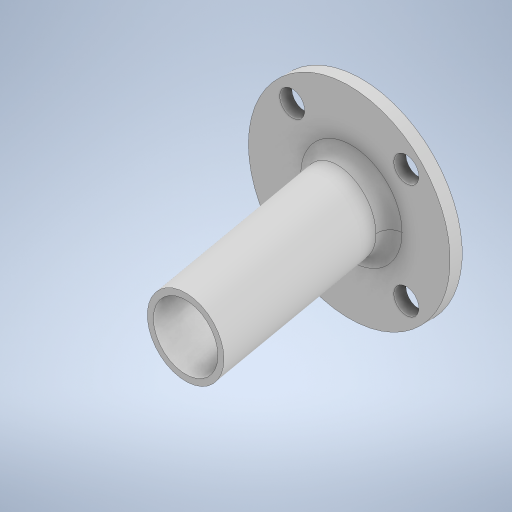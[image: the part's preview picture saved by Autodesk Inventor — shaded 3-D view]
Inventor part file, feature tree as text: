
AUTODESK INVENTOR PART (.ipt)
format: ipt  version: 2023 (Build 270158000, 158)  size: 305,664 bytes
history: native  units: in
note: dims shown in document units (in); Inventor stores cm internally (conversion verified against a paired STEP export)
features: sketch x5, sweep x2, extrude x1, fillet x1
ambient origin geometry x8: Origin, YZ Plane, XZ Plane, XY Plane, X Axis, Y Axis, Z Axis, Center Point
bodies: Solid1 (feature_tree)
feature tree (9):
  extrude  "Extrusion1"  Depth=0.2461in
  sweep  "Sweep4"
  sweep  "Sweep5"
  fillet  "Fillet2"  Radius=0.748in
  sketch  "Sketch2"  dims[d0=1.9685in d10=0.2461in]
  sketch  "Sketch19"  dims[d11=0.2461in d12=0.2461in]
  sketch  "Sketch22"  dims[d13=0.2461in d14=0.1181in d15=0.0in d40=0.748in]
  sketch  "Sketch23"  dims[d41=1.9685in]
  sketch  "Sketch25"  dims[d42=0.6871in d43=0.0in d44=0.0in d45=0.6299in d46=1.9685in d47=0.6871in d48=0.0in d49=0.0in d50=0.1181in]
